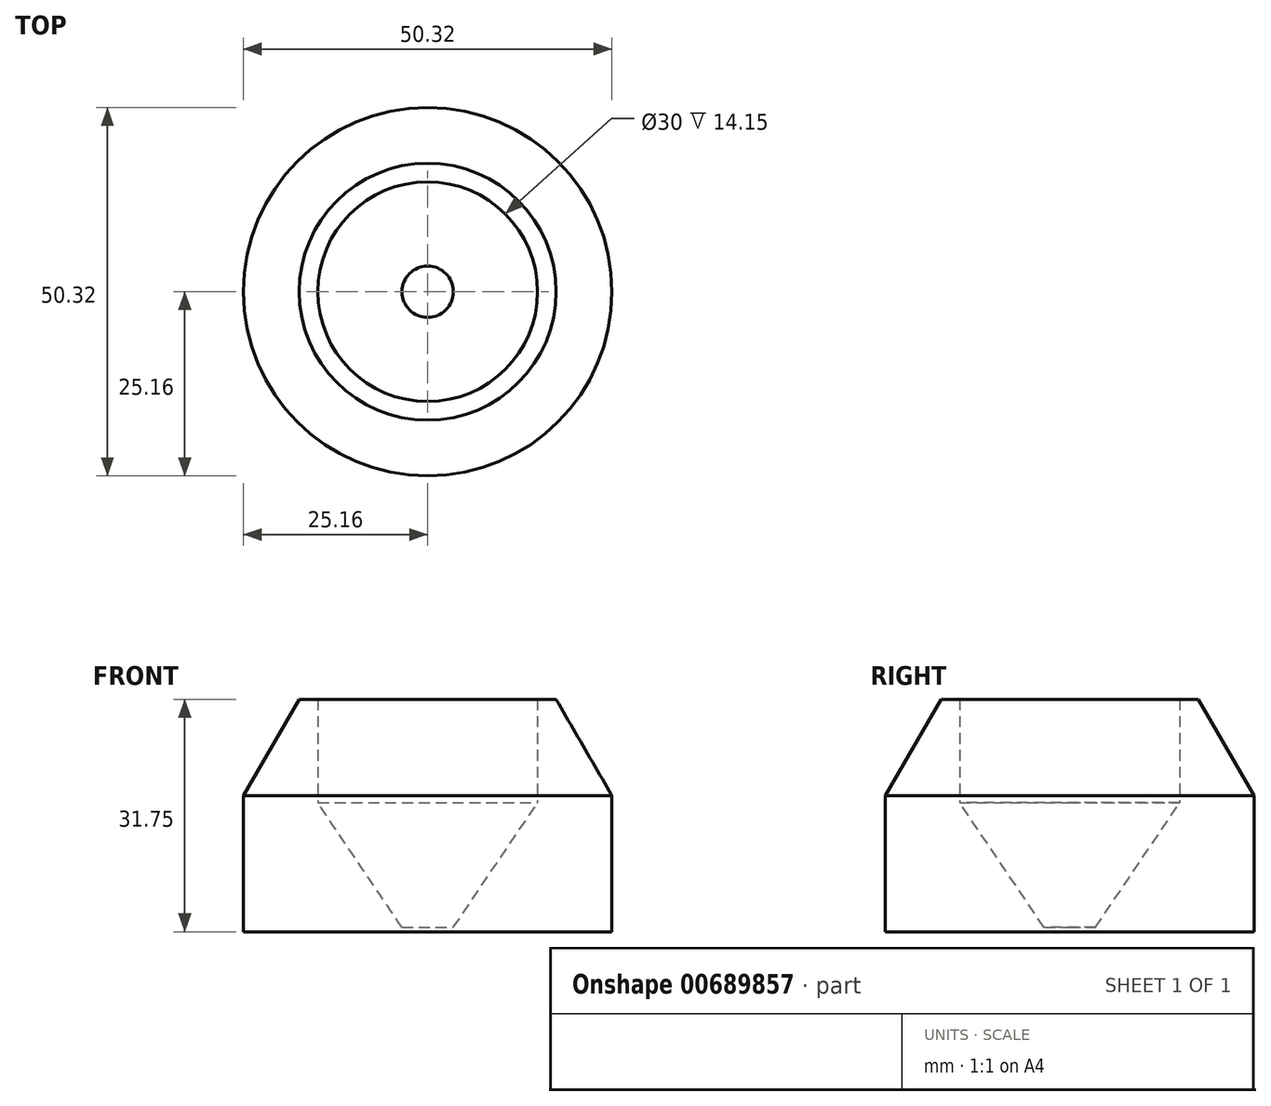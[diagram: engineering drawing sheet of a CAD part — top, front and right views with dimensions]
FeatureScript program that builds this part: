
annotation { "Feature Type Name" : "Feature", "Feature Type Description" : "" }
export const myFeature = defineFeature(function(context is Context, id is Id, definition is map)
    precondition{}
    {
        {
            var Q0;
            Q0=qCreatedBy(makeId("Top.planeOp"),FACE);
            var sketch = newSketch(context, id + "F0", { "sketchPlane" : qUnion([Q0])});
            skCircle(sketch, "E0", {"center": v(0, 0) * mm, "radius": 50.68 * mm});
            skSolve(sketch);
        }
        {
            var Q0;
            Q0 = qSketchRegion(id + "F0", true);
            extrude(context, id + "F1", {"entities" : qUnion([Q0]), "depth" : 95.25 * mm, "offsetDistance" : 25.4 * mm});
        }
        {
            var Q0;
            Q0=qCreatedBy(makeId("Front.planeOp"),FACE);
            var sketch = newSketch(context, id + "F2", { "sketchPlane" : qUnion([Q0])});
            skLineSegment(sketch, "E1", {"start": v(0, 0) * mm, "end": v(-31.75, 0) * mm});
            skLineSegment(sketch, "E2", {"start": v(-31.75, 0) * mm, "end": v(-50.7, 12.7) * mm});
            skLineSegment(sketch, "E3", {"start": v(-50.7, 12.7) * mm, "end": v(-50.7, 0) * mm});
            skLineSegment(sketch, "E4", {"start": v(-50.7, 0) * mm, "end": v(-31.75, 0) * mm});
            skLineSegment(sketch, "E5", {"start": v(0, 0) * mm, "end": v(0, 42.12) * mm});
            skSolve(sketch);
        }
        {
            var Q0;
            Q0 = qSketchRegion(id + "F2", true);
            var Q1;
            Q1=sQuery(id+"F2.wireOp",EDGE,"E5");
            revolve(context, id + "F3", {"operationType" : NewBodyOperationType.REMOVE, "surfaceOperationType" : NewSurfaceOperationType.NEW, "entities" : qUnion([Q0]), "axis" : qUnion([Q1]), "revolveType" : RevolveType.FULL, "oppositeDirection" : true});
        }
        {
            var Q0;
            Q0=qCreatedBy(makeId("Front.planeOp"),FACE);
            var sketch = newSketch(context, id + "F4", { "sketchPlane" : qUnion([Q0])});
            skLineSegment(sketch, "E6", {"start": v(0, 108.29) * mm, "end": v(0, 0.6) * mm});
            skLineSegment(sketch, "E7", {"start": v(0, 0.6) * mm, "end": v(-3.5, 0.6) * mm});
            skLineSegment(sketch, "E8", {"start": v(-3.5, 0.6) * mm, "end": v(-15, 17.6) * mm});
            skLineSegment(sketch, "E9", {"start": v(-15, 17.6) * mm, "end": v(-15, 108.29) * mm});
            skLineSegment(sketch, "E10", {"start": v(-15, 108.29) * mm, "end": v(0, 108.29) * mm});
            skSolve(sketch);
        }
        {
            var Q0;
            Q0=makeQuery(id+"F4.imprint","IMPRINT",FACE,{"disambiguationData":[TD([[makeQuery(id+"F4.imprint","IMPRINT",EDGE,{"derivedFrom":sQuery(id+"F4.wireOp",EDGE,"E6")}),-1.0]])]});
            var Q1;
            Q1=sQuery(id+"F4.wireOp",EDGE,"E6");
            revolve(context, id + "F5", {"operationType" : NewBodyOperationType.REMOVE, "surfaceOperationType" : NewSurfaceOperationType.NEW, "entities" : qUnion([Q0]), "axis" : qUnion([Q1]), "revolveType" : RevolveType.FULL, "oppositeDirection" : true});
        }
        {
            var Q0;
            Q0=makeQuery(id+"F1.opExtrude","CAP_FACE",FACE,{"disambiguationData":[OSD([sQuery(id+"F0.wireOp",EDGE,"E0")])],"isStart":false});
            var sketch = newSketch(context, id + "F6", { "sketchPlane" : qUnion([Q0])});
            skCircle(sketch, "E11", {"center": v(0, 0) * mm, "radius": 64.25 * mm});
            skSolve(sketch);
        }
        {
            var Q0;
            Q0 = qSketchRegion(id + "F6", true);
            extrude(context, id + "F7", {"entities" : qUnion([Q0]), "operationType" : NewBodyOperationType.REMOVE, "oppositeDirection" : true, "depth" : 63.5 * mm, "offsetDistance" : 25.4 * mm});
        }
        {
            var Q0;
            Q0=makeQuery(id+"F1.opExtrude","CAP_FACE",FACE,{"disambiguationData":[OSD([sQuery(id+"F0.wireOp",EDGE,"E0")])],"isStart":true});
            var sketch = newSketch(context, id + "F8", { "sketchPlane" : qUnion([Q0])});
            skCircle(sketch, "E12", {"center": v(0, 0) * mm, "radius": 25.16 * mm});
            skCircle(sketch, "E13", {"center": v(0, 0) * mm, "radius": 77.3 * mm});
            skSolve(sketch);
        }
        {
            var Q0;
            Q0=makeQuery(id+"F7.boolean.opBoolean","COPY",FACE,{"derivedFrom":makeQuery(id+"F7.opExtrude","CAP_FACE",FACE,{"disambiguationData":[OSD([sQuery(id+"F6.wireOp",EDGE,"E11")])],"isStart":false})});
            var sketch = newSketch(context, id + "F9", { "sketchPlane" : qUnion([Q0])});
            skArc(sketch, "E14", {"start": v(11.7, 25.1) * mm, "mid": v(0, 27.7) * mm, "end": v(-11.7, 25.1) * mm});
            skArc(sketch, "E15", {"start": v(19.27, 41.32) * mm, "mid": v(0, 45.6) * mm, "end": v(-19.27, 41.32) * mm});
            skLineSegment(sketch, "E16", {"start": v(-11.7, 25.1) * mm, "end": v(-19.27, 41.32) * mm});
            skLineSegment(sketch, "E17", {"start": v(11.7, 25.1) * mm, "end": v(19.27, 41.32) * mm});
            skLineSegment(sketch, "E18", {"start": v(-19.27, 41.32) * mm, "end": v(19.27, 41.32) * mm, "construction": true});
            skLineSegment(sketch, "E19.1.0", {"start": v(-20.26, 18.9) * mm, "end": v(-33.35, 31.1) * mm});
            skArc(sketch, "E19.1.1", {"start": v(-33.35, 31.1) * mm, "mid": v(-43.36, 14.09) * mm, "end": v(-45.26, -5.56) * mm});
            skLineSegment(sketch, "E19.1.2", {"start": v(-27.5, -3.38) * mm, "end": v(-45.26, -5.56) * mm});
            skLineSegment(sketch, "E19.1.3", {"start": v(-45.26, -5.56) * mm, "end": v(-33.35, 31.1) * mm, "construction": true});
            skArc(sketch, "E19.1.4", {"start": v(-20.26, 18.9) * mm, "mid": v(-26.34, 8.56) * mm, "end": v(-27.5, -3.38) * mm});
            skLineSegment(sketch, "E19.2.0", {"start": v(-24.23, -13.43) * mm, "end": v(-39.88, -22.1) * mm});
            skArc(sketch, "E19.2.1", {"start": v(-39.88, -22.1) * mm, "mid": v(-26.8, -36.89) * mm, "end": v(-8.7, -44.76) * mm});
            skLineSegment(sketch, "E19.2.2", {"start": v(-5.29, -27.2) * mm, "end": v(-8.7, -44.76) * mm});
            skLineSegment(sketch, "E19.2.3", {"start": v(-8.7, -44.76) * mm, "end": v(-39.88, -22.1) * mm, "construction": true});
            skArc(sketch, "E19.2.4", {"start": v(-24.23, -13.43) * mm, "mid": v(-16.28, -22.4) * mm, "end": v(-5.29, -27.2) * mm});
            skLineSegment(sketch, "E19.3.0", {"start": v(5.29, -27.2) * mm, "end": v(8.7, -44.76) * mm});
            skArc(sketch, "E19.3.1", {"start": v(8.7, -44.76) * mm, "mid": v(26.8, -36.89) * mm, "end": v(39.88, -22.1) * mm});
            skLineSegment(sketch, "E19.3.2", {"start": v(24.23, -13.43) * mm, "end": v(39.88, -22.1) * mm});
            skLineSegment(sketch, "E19.3.3", {"start": v(39.88, -22.1) * mm, "end": v(8.7, -44.76) * mm, "construction": true});
            skArc(sketch, "E19.3.4", {"start": v(5.29, -27.2) * mm, "mid": v(16.28, -22.4) * mm, "end": v(24.23, -13.43) * mm});
            skLineSegment(sketch, "E19.4.0", {"start": v(27.5, -3.38) * mm, "end": v(45.26, -5.56) * mm});
            skArc(sketch, "E19.4.1", {"start": v(45.26, -5.56) * mm, "mid": v(43.36, 14.09) * mm, "end": v(33.35, 31.1) * mm});
            skLineSegment(sketch, "E19.4.2", {"start": v(20.26, 18.9) * mm, "end": v(33.35, 31.1) * mm});
            skLineSegment(sketch, "E19.4.3", {"start": v(33.35, 31.1) * mm, "end": v(45.26, -5.56) * mm, "construction": true});
            skArc(sketch, "E19.4.4", {"start": v(27.5, -3.38) * mm, "mid": v(26.34, 8.56) * mm, "end": v(20.26, 18.9) * mm});
            skSolve(sketch);
        }
        {
            var Q0;
            Q0 = qSketchRegion(id + "F9", true);
            extrude(context, id + "F10", {"entities" : qUnion([Q0]), "operationType" : NewBodyOperationType.REMOVE, "endBound" : BoundingType.THROUGH_ALL, "oppositeDirection" : true, "depth" : 25.4 * mm, "offsetDistance" : 25.4 * mm});
        }
        {
            var Q0;
            Q0 = qSketchRegion(id + "F8", true);
            extrude(context, id + "F11", {"entities" : qUnion([Q0]), "operationType" : NewBodyOperationType.REMOVE, "endBound" : BoundingType.THROUGH_ALL, "oppositeDirection" : true, "depth" : 25.4 * mm, "offsetDistance" : 25.4 * mm});
        }
        {
            var Q0;
            Q0=makeQuery(id+"F11.boolean.opBoolean","INTERSECT",EDGE,{"derivedFrom":[makeQuery(id+"F7.boolean.opBoolean","COPY",FACE,{"derivedFrom":makeQuery(id+"F7.opExtrude","CAP_FACE",FACE,{"disambiguationData":[OSD([sQuery(id+"F6.wireOp",EDGE,"E11")])],"isStart":false})}),makeQuery(id+"F11.opExtrude","SWEPT_FACE",FACE,{"disambiguationData":[OSD([sQuery(id+"F8.wireOp",EDGE,"E12")])]})]});
            chamfer(context, id + "F12", {"entities" : qUnion([Q0]), "chamferType" : ChamferType.OFFSET_ANGLE, "width" : 7.62 * mm, "oppositeDirection" : false, "angle" : 60 * degree, "tangentPropagation" : true});
        }
    });
